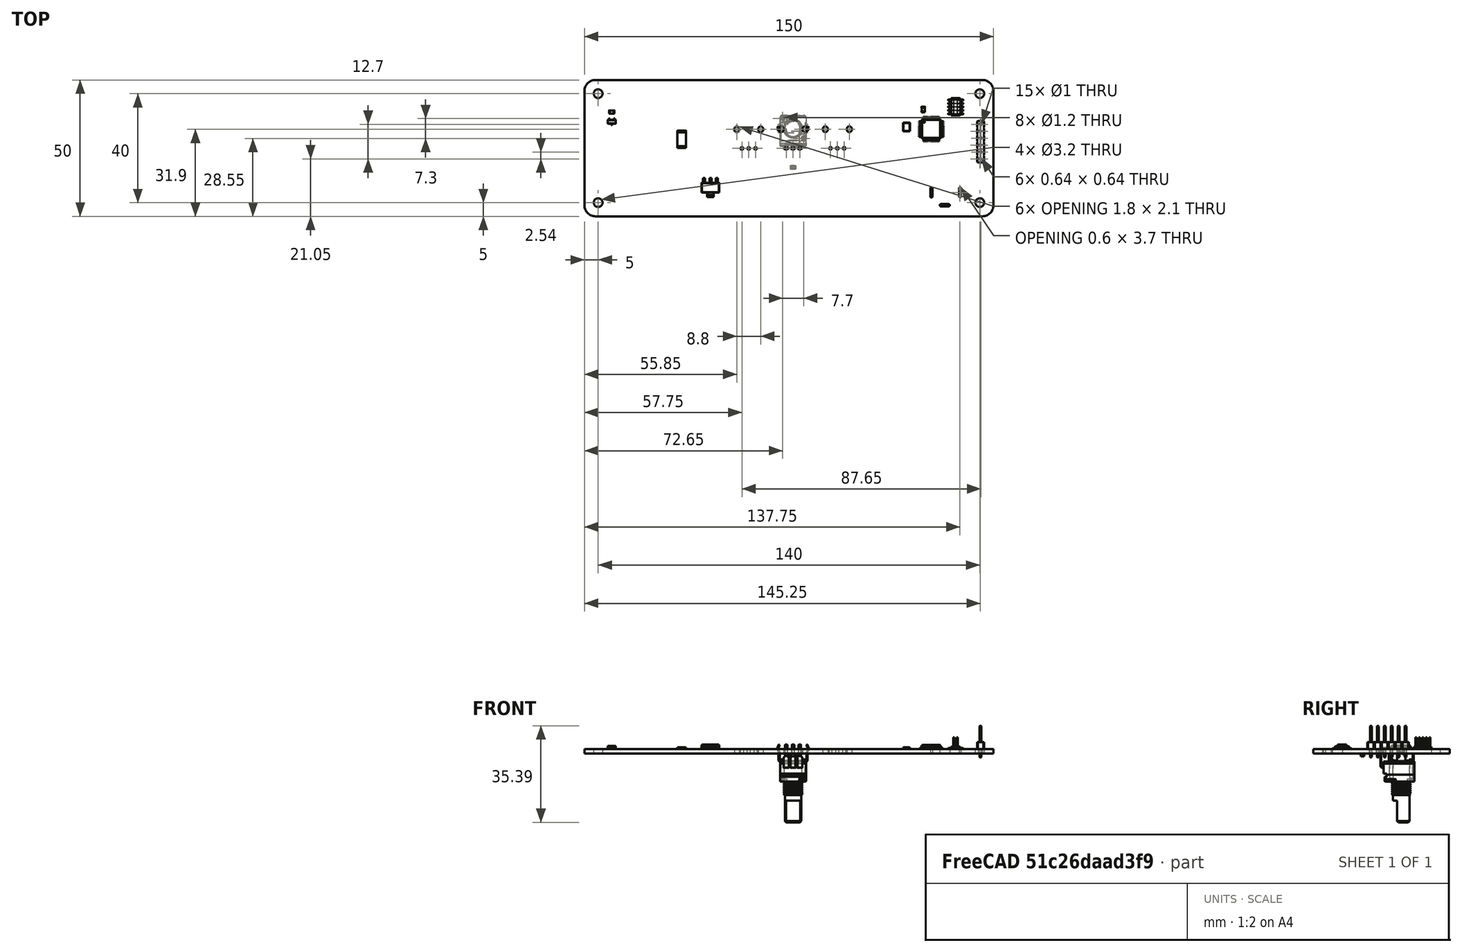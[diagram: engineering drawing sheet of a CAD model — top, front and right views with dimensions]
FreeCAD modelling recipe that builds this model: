
FCSTD DOCUMENT  (FreeCAD 0.19R24291 (Git))
Label: pcb
License: All rights reserved
LicenseURL: http://en.wikipedia.org/wiki/All_rights_reserved
objects: App::Link×47, Part::Feature×12, App::Part×5, PartDesign::CoordinateSystem×1, Sketcher::SketchObject×1
note: 14 computed .brp shape members not serialized (recipe doc carries the construction recipe); baked Part::Feature solids carry a one-line shape summary decoded from their .brp

FEATURE [PartDesign::CoordinateSystem] Local_CS_2cbe
  AttacherType = Attacher::AttachEngine3D
FEATURE [Part::Feature] Pcb_2cbe
  shape: bbox 150 x 50 x 1.6 mm, 83 faces (baked)
FEATURE [Sketcher::SketchObject] PCB_Sketch_2cbe
  FullyConstrained = false
  sketch-geometry (8):
    g0: LineSegment StartX=150 StartY=-46 StartZ=0 EndX=150 EndY=-4 EndZ=0
    g1: LineSegment StartX=4 StartY=-50 StartZ=0 EndX=146 EndY=-50 EndZ=0
    g2: LineSegment StartX=146 StartY=-4.4e-15 StartZ=0 EndX=4 EndY=0 EndZ=0
    g3: LineSegment StartX=0 StartY=-4 StartZ=0 EndX=4.4e-15 EndY=-46 EndZ=0
    g4: ArcOfCircle CenterX=146 CenterY=-46 CenterZ=0 NormalX=0 NormalY=0 NormalZ=-1 AngleXU=-3.14159 Radius=4 StartAngle=0 EndAngle=1.5708
    g5: ArcOfCircle CenterX=4 CenterY=-4 CenterZ=0 NormalX=0 NormalY=0 NormalZ=-1 AngleXU=1.06478e-07 Radius=4 StartAngle=0 EndAngle=1.5708
    g6: ArcOfCircle CenterX=146 CenterY=-4 CenterZ=0 NormalX=0 NormalY=0 NormalZ=-1 AngleXU=1.5708 Radius=4 StartAngle=0 EndAngle=1.5708
    g7: ArcOfCircle CenterX=4 CenterY=-46 CenterZ=0 NormalX=0 NormalY=0 NormalZ=-1 AngleXU=-1.5708 Radius=4 StartAngle=0 EndAngle=1.5708
  constraints (8):
    c: Coincident(g3,g7)
    c: Coincident(g3,g5)
    c: Coincident(g7,g1)
    c: Coincident(g2,g5)
    c: Coincident(g4,g1)
    c: Coincident(g6,g2)
    c: Coincident(g0,g4)
    c: Coincident(g0,g6)
FEATURE [App::Part] Board_Geoms_2cbe
  Group = -> [Local_CS_2cbe,Pcb_2cbe,PCB_Sketch_2cbe]
  Origin = -> Origin
FEATURE [Part::Feature] Shape  label="U3_SOT_223_9a0cac0f9152"
  Placement = pos=(46.1875,-39.5,0) rot=(0,0,-1;1.5708rad)
  shape: bbox 6.5 x 7 x 1.7 mm, 78 faces (baked)
FEATURE [Part::Feature] Shape001  label="R17_R_0805_2012Metric_1d3dcb9a6ad1"
  Placement = pos=(10,-11.75,0) rot=(0,0,1;3.14159rad)
  shape: bbox 2 x 1.2 x 0.45 mm, 26 faces (baked)
FEATURE [App::Link] R17_R_0805_2012Metric_1d3dcb9a6ad1_ln_  label="R11_R_0805_2012Metric_20203f5f4346"
  LinkPlacement = pos=(20.25,-11.75,0) rot=(0,0,1;3.14159rad)
  LinkedObject = -> Shape001
  Placement = pos=(20.25,-11.75,0) rot=(0,0,1;3.14159rad)
FEATURE [Part::Feature] Shape002  label="R3_R_2512_6332Metric_9794fe5d1dc9"
  Placement = pos=(35.6875,-21.75,0) rot=(0,0,1;1.5708rad)
  shape: bbox 3.2 x 6.3 x 0.6 mm, 26 faces (baked)
FEATURE [App::Link] R17_R_0805_2012Metric_1d3dcb9a6ad1_ln_001  label="R14_R_0805_2012Metric_fdd2a95da5c4"
  LinkPlacement = pos=(15,-11.75,0) rot=(0,0,1;3.14159rad)
  LinkedObject = -> Shape001
  Placement = pos=(15,-11.75,0) rot=(0,0,1;3.14159rad)
FEATURE [Part::Feature] Shape003  label="C5_C_0805_2012Metric_e73408091e88"
  Placement = pos=(124.25,-10.8,0) rot=(0,0,1;1.5708rad)
  shape: bbox 1.25 x 2 x 1.25 mm, 28 faces (baked)
FEATURE [App::Link] R17_R_0805_2012Metric_1d3dcb9a6ad1_ln_002  label="R25_R_0805_2012Metric_45299f0951f4"
  LinkPlacement = pos=(41.1875,-9.25,0) rot=(0,0,1;0rad)
  LinkedObject = -> Shape001
  Placement = pos=(41.1875,-9.25,0) rot=(0,0,1;0rad)
FEATURE [App::Link] R3_R_2512_6332Metric_9794fe5d1dc9_ln_  label="R21_R_2512_6332Metric_ab6f071dc77f"
  LinkPlacement = pos=(51.4375,-21.75,0) rot=(0,0,1;1.5708rad)
  LinkedObject = -> Shape002
  Placement = pos=(51.4375,-21.75,0) rot=(0,0,1;1.5708rad)
FEATURE [Part::Feature] Shape004  label="Q6_SOT_23_5775dbb67c7d"
  Placement = pos=(10,-15.3125,0) rot=(0,0,-1;1.5708rad)
  shape: bbox 3 x 2.5 x 1.2 mm, 76 faces (baked)
FEATURE [App::Link] R17_R_0805_2012Metric_1d3dcb9a6ad1_ln_003  label="R20_R_0805_2012Metric_a0866f91f469"
  LinkPlacement = pos=(51.4375,-11.75,0) rot=(0,0,1;3.14159rad)
  LinkedObject = -> Shape001
  Placement = pos=(51.4375,-11.75,0) rot=(0,0,1;3.14159rad)
FEATURE [App::Link] R17_R_0805_2012Metric_1d3dcb9a6ad1_ln_004  label="R22_R_0805_2012Metric_833be10c83fc"
  LinkPlacement = pos=(46.1875,-9.25,0) rot=(0,0,1;0rad)
  LinkedObject = -> Shape001
  Placement = pos=(46.1875,-9.25,0) rot=(0,0,1;0rad)
FEATURE [App::Link] R3_R_2512_6332Metric_9794fe5d1dc9_ln_001  label="R18_R_2512_6332Metric_0a6bf79341f9"
  LinkPlacement = pos=(10,-21.75,0) rot=(0,0,1;1.5708rad)
  LinkedObject = -> Shape002
  Placement = pos=(10,-21.75,0) rot=(0,0,1;1.5708rad)
FEATURE [App::Link] R17_R_0805_2012Metric_1d3dcb9a6ad1_ln_005  label="R19_R_0805_2012Metric_baaa63a81d46"
  LinkPlacement = pos=(51.4375,-9.25,0) rot=(0,0,1;0rad)
  LinkedObject = -> Shape001
  Placement = pos=(51.4375,-9.25,0) rot=(0,0,1;0rad)
FEATURE [App::Link] R17_R_0805_2012Metric_1d3dcb9a6ad1_ln_006  label="R10_R_0805_2012Metric_2b905bbe2cce"
  LinkPlacement = pos=(20.25,-9.25,0) rot=(0,0,1;0rad)
  LinkedObject = -> Shape001
  Placement = pos=(20.25,-9.25,0) rot=(0,0,1;0rad)
FEATURE [App::Link] C5_C_0805_2012Metric_e73408091e88_ln_  label="C1_C_0805_2012Metric_e32d38fff6b7"
  LinkPlacement = pos=(118.25,-20.8,0) rot=(0,0,1;3.14159rad)
  LinkedObject = -> Shape003
  Placement = pos=(118.25,-20.8,0) rot=(0,0,1;3.14159rad)
FEATURE [App::Link] C5_C_0805_2012Metric_e73408091e88_ln_001  label="C7_C_0805_2012Metric_6d577f5282f8"
  LinkPlacement = pos=(132,-23.5,0) rot=(0,0,-1;1.5708rad)
  LinkedObject = -> Shape003
  Placement = pos=(132,-23.5,0) rot=(0,0,-1;1.5708rad)
FEATURE [App::Link] Q6_SOT_23_5775dbb67c7d_ln_  label="Q9_SOT_23_ff8b5d4c65c8"
  LinkPlacement = pos=(41.1875,-15.3125,0) rot=(0,0,-1;1.5708rad)
  LinkedObject = -> Shape004
  Placement = pos=(41.1875,-15.3125,0) rot=(0,0,-1;1.5708rad)
FEATURE [App::Link] U3_SOT_223_9a0cac0f9152_ln_  label="U4_SOT_223_e91abe411a87"
  LinkPlacement = pos=(137.85,-32.85,0) rot=(0,0,1;0rad)
  LinkedObject = -> Shape
  Placement = pos=(137.85,-32.85,0) rot=(0,0,1;0rad)
FEATURE [App::Link] C5_C_0805_2012Metric_e73408091e88_ln_002  label="C4_C_0805_2012Metric_672b2dcb80fa"
  LinkPlacement = pos=(137,-23.5,0) rot=(0,0,-1;1.5708rad)
  LinkedObject = -> Shape003
  Placement = pos=(137,-23.5,0) rot=(0,0,-1;1.5708rad)
FEATURE [App::Link] Q6_SOT_23_5775dbb67c7d_ln_001  label="Q7_SOT_23_17abb1841a15"
  LinkPlacement = pos=(51.4375,-15.3125,0) rot=(0,0,-1;1.5708rad)
  LinkedObject = -> Shape004
  Placement = pos=(51.4375,-15.3125,0) rot=(0,0,-1;1.5708rad)
FEATURE [App::Link] R3_R_2512_6332Metric_9794fe5d1dc9_ln_002  label="R15_R_2512_6332Metric_e9b0cec35db8"
  LinkPlacement = pos=(15,-21.75,0) rot=(0,0,1;1.5708rad)
  LinkedObject = -> Shape002
  Placement = pos=(15,-21.75,0) rot=(0,0,1;1.5708rad)
FEATURE [App::Link] R3_R_2512_6332Metric_9794fe5d1dc9_ln_003  label="R27_R_2512_6332Metric_f9a6948b6ee0"
  LinkPlacement = pos=(41.1875,-21.75,0) rot=(0,0,1;1.5708rad)
  LinkedObject = -> Shape002
  Placement = pos=(41.1875,-21.75,0) rot=(0,0,1;1.5708rad)
FEATURE [App::Link] R17_R_0805_2012Metric_1d3dcb9a6ad1_ln_007  label="R2_R_0805_2012Metric_4f3d63e405d4"
  LinkPlacement = pos=(35.6875,-11.75,0) rot=(0,0,1;3.14159rad)
  LinkedObject = -> Shape001
  Placement = pos=(35.6875,-11.75,0) rot=(0,0,1;3.14159rad)
FEATURE [App::Link] U3_SOT_223_9a0cac0f9152_ln_001  label="U1_SOT_223_7fe5ee313dd0"
  LinkPlacement = pos=(30.4375,-39.5,0) rot=(0,0,-1;1.5708rad)
  LinkedObject = -> Shape
  Placement = pos=(30.4375,-39.5,0) rot=(0,0,-1;1.5708rad)
FEATURE [App::Link] R3_R_2512_6332Metric_9794fe5d1dc9_ln_004  label="R9_R_2512_6332Metric_ee968ef2a15d"
  LinkPlacement = pos=(25.4375,-21.75,0) rot=(0,0,1;1.5708rad)
  LinkedObject = -> Shape002
  Placement = pos=(25.4375,-21.75,0) rot=(0,0,1;1.5708rad)
FEATURE [App::Link] R17_R_0805_2012Metric_1d3dcb9a6ad1_ln_008  label="R28_R_0805_2012Metric_0c4fd54d4787"
  LinkPlacement = pos=(130.5,-8.4125,0) rot=(0,0,1;1.5708rad)
  LinkedObject = -> Shape001
  Placement = pos=(130.5,-8.4125,0) rot=(0,0,1;1.5708rad)
FEATURE [App::Link] R3_R_2512_6332Metric_9794fe5d1dc9_ln_005  label="R6_R_2512_6332Metric_ac73445917ac"
  LinkPlacement = pos=(30.4375,-21.75,0) rot=(0,0,1;1.5708rad)
  LinkedObject = -> Shape002
  Placement = pos=(30.4375,-21.75,0) rot=(0,0,1;1.5708rad)
FEATURE [App::Link] R17_R_0805_2012Metric_1d3dcb9a6ad1_ln_009  label="R8_R_0805_2012Metric_5f2fab4355a1"
  LinkPlacement = pos=(25.4375,-11.75,0) rot=(0,0,1;3.14159rad)
  LinkedObject = -> Shape001
  Placement = pos=(25.4375,-11.75,0) rot=(0,0,1;3.14159rad)
FEATURE [App::Link] R17_R_0805_2012Metric_1d3dcb9a6ad1_ln_010  label="R29_R_0805_2012Metric_2565f2ac43fa"
  LinkPlacement = pos=(135.25,-20,0) rot=(0,0,1;0rad)
  LinkedObject = -> Shape001
  Placement = pos=(135.25,-20,0) rot=(0,0,1;0rad)
FEATURE [App::Link] R17_R_0805_2012Metric_1d3dcb9a6ad1_ln_011  label="R23_R_0805_2012Metric_bd181034dc98"
  LinkPlacement = pos=(46.1875,-11.75,0) rot=(0,0,1;3.14159rad)
  LinkedObject = -> Shape001
  Placement = pos=(46.1875,-11.75,0) rot=(0,0,1;3.14159rad)
FEATURE [App::Link] C5_C_0805_2012Metric_e73408091e88_ln_003  label="C8_C_0805_2012Metric_dd346f149829"
  LinkPlacement = pos=(131.25,-34.8,0) rot=(0,0,-1;1.5708rad)
  LinkedObject = -> Shape003
  Placement = pos=(131.25,-34.8,0) rot=(0,0,-1;1.5708rad)
FEATURE [Part::Feature] Shape005  label="Y1_Crystal_SMD_3225-4Pin_3.2x2.5mm_c7f48e4b8aec"
  Placement = pos=(118.15,-17.2,0) rot=(0,0,-1;1.5708rad)
  shape: bbox 2.501 x 3.2 x 0.64 mm, 28 faces (baked)
FEATURE [Part::Feature] Shape006  label="J5_PinHeader_2x05_P127mm_Vertical_SMD_d72e22a41a84"
  Placement = pos=(136.15,-9.85,0) rot=(0,0,1;3.14159rad)
  shape: bbox 5.57 x 6.35 x 4.4 mm, 224 faces (baked)
FEATURE [App::Link] C5_C_0805_2012Metric_e73408091e88_ln_004  label="C2_C_0805_2012Metric_1cae6d697659"
  LinkPlacement = pos=(118.2,-13.8,0) rot=(0,0,1;3.14159rad)
  LinkedObject = -> Shape003
  Placement = pos=(118.2,-13.8,0) rot=(0,0,1;3.14159rad)
FEATURE [Part::Feature] Shape007  label="J6_PinHeader_1x06_P254mm_Vertical_fd384cb3f28f"
  Placement = pos=(145.25,-16.25,0) rot=(0,0,1;0rad)
  shape: bbox 2.54 x 15.24 x 11.54 mm, 148 faces (baked)
FEATURE [App::Link] R3_R_2512_6332Metric_9794fe5d1dc9_ln_006  label="R24_R_2512_6332Metric_24b84e4ca8f6"
  LinkPlacement = pos=(46.1875,-21.75,0) rot=(0,0,1;1.5708rad)
  LinkedObject = -> Shape002
  Placement = pos=(46.1875,-21.75,0) rot=(0,0,1;1.5708rad)
FEATURE [App::Link] R17_R_0805_2012Metric_1d3dcb9a6ad1_ln_012  label="R26_R_0805_2012Metric_8c81e733eccd"
  LinkPlacement = pos=(41.1875,-11.75,0) rot=(0,0,1;3.14159rad)
  LinkedObject = -> Shape001
  Placement = pos=(41.1875,-11.75,0) rot=(0,0,1;3.14159rad)
FEATURE [App::Link] Q6_SOT_23_5775dbb67c7d_ln_002  label="Q8_SOT_23_1fa8c5138ddd"
  LinkPlacement = pos=(46.1875,-15.3125,0) rot=(0,0,-1;1.5708rad)
  LinkedObject = -> Shape004
  Placement = pos=(46.1875,-15.3125,0) rot=(0,0,-1;1.5708rad)
FEATURE [App::Link] Q6_SOT_23_5775dbb67c7d_ln_003  label="Q5_SOT_23_a44b0229e8dc"
  LinkPlacement = pos=(15,-15.3125,0) rot=(0,0,-1;1.5708rad)
  LinkedObject = -> Shape004
  Placement = pos=(15,-15.3125,0) rot=(0,0,-1;1.5708rad)
FEATURE [App::Link] C5_C_0805_2012Metric_e73408091e88_ln_005  label="C3_C_0805_2012Metric_4d4c3b780c7d"
  LinkPlacement = pos=(134.5,-23.5,0) rot=(0,0,-1;1.5708rad)
  LinkedObject = -> Shape003
  Placement = pos=(134.5,-23.5,0) rot=(0,0,-1;1.5708rad)
FEATURE [App::Link] Q6_SOT_23_5775dbb67c7d_ln_004  label="Q1_SOT_23_beec94fd2b5f"
  LinkPlacement = pos=(35.6875,-15.3125,0) rot=(0,0,-1;1.5708rad)
  LinkedObject = -> Shape004
  Placement = pos=(35.6875,-15.3125,0) rot=(0,0,-1;1.5708rad)
FEATURE [App::Link] R17_R_0805_2012Metric_1d3dcb9a6ad1_ln_013  label="R5_R_0805_2012Metric_c2fdd37d7649"
  LinkPlacement = pos=(30.4375,-11.75,0) rot=(0,0,1;3.14159rad)
  LinkedObject = -> Shape001
  Placement = pos=(30.4375,-11.75,0) rot=(0,0,1;3.14159rad)
FEATURE [App::Link] R17_R_0805_2012Metric_1d3dcb9a6ad1_ln_014  label="R30_R_0805_2012Metric_f70d4868c63e"
  LinkPlacement = pos=(126.5,-10.75,0) rot=(0,0,1;1.5708rad)
  LinkedObject = -> Shape001
  Placement = pos=(126.5,-10.75,0) rot=(0,0,1;1.5708rad)
FEATURE [App::Link] R17_R_0805_2012Metric_1d3dcb9a6ad1_ln_015  label="R4_R_0805_2012Metric_136d3f58f10c"
  LinkPlacement = pos=(30.4375,-9.25,0) rot=(0,0,1;0rad)
  LinkedObject = -> Shape001
  Placement = pos=(30.4375,-9.25,0) rot=(0,0,1;0rad)
FEATURE [App::Link] R17_R_0805_2012Metric_1d3dcb9a6ad1_ln_016  label="R7_R_0805_2012Metric_8f9a76bd2325"
  LinkPlacement = pos=(25.4375,-9.25,0) rot=(0,0,1;0rad)
  LinkedObject = -> Shape001
  Placement = pos=(25.4375,-9.25,0) rot=(0,0,1;0rad)
FEATURE [App::Link] R17_R_0805_2012Metric_1d3dcb9a6ad1_ln_017  label="R1_R_0805_2012Metric_98cd4f012b1e"
  LinkPlacement = pos=(35.6875,-9.25,0) rot=(0,0,1;0rad)
  LinkedObject = -> Shape001
  Placement = pos=(35.6875,-9.25,0) rot=(0,0,1;0rad)
FEATURE [App::Link] R17_R_0805_2012Metric_1d3dcb9a6ad1_ln_018  label="R13_R_0805_2012Metric_5c4c1cf987fe"
  LinkPlacement = pos=(15,-9.25,0) rot=(0,0,1;0rad)
  LinkedObject = -> Shape001
  Placement = pos=(15,-9.25,0) rot=(0,0,1;0rad)
FEATURE [App::Link] R3_R_2512_6332Metric_9794fe5d1dc9_ln_007  label="R12_R_2512_6332Metric_5527fe2de375"
  LinkPlacement = pos=(20.25,-21.75,0) rot=(0,0,1;1.5708rad)
  LinkedObject = -> Shape002
  Placement = pos=(20.25,-21.75,0) rot=(0,0,1;1.5708rad)
FEATURE [App::Link] Q6_SOT_23_5775dbb67c7d_ln_005  label="Q4_SOT_23_f877d4d9137f"
  LinkPlacement = pos=(20.25,-15.3125,0) rot=(0,0,-1;1.5708rad)
  LinkedObject = -> Shape004
  Placement = pos=(20.25,-15.3125,0) rot=(0,0,-1;1.5708rad)
FEATURE [App::Link] Q6_SOT_23_5775dbb67c7d_ln_006  label="Q2_SOT_23_ab36755b93e8"
  LinkPlacement = pos=(30.4375,-15.3125,0) rot=(0,0,-1;1.5708rad)
  LinkedObject = -> Shape004
  Placement = pos=(30.4375,-15.3125,0) rot=(0,0,-1;1.5708rad)
FEATURE [App::Link] R17_R_0805_2012Metric_1d3dcb9a6ad1_ln_019  label="R16_R_0805_2012Metric_7f67fb58ddc2"
  LinkPlacement = pos=(10,-9.25,0) rot=(0,0,1;0rad)
  LinkedObject = -> Shape001
  Placement = pos=(10,-9.25,0) rot=(0,0,1;0rad)
FEATURE [App::Link] C5_C_0805_2012Metric_e73408091e88_ln_006  label="C6_C_0805_2012Metric_12e3dac60f4f"
  LinkPlacement = pos=(122,-12.8,0) rot=(0,0,1;1.5708rad)
  LinkedObject = -> Shape003
  Placement = pos=(122,-12.8,0) rot=(0,0,1;1.5708rad)
FEATURE [App::Link] Q6_SOT_23_5775dbb67c7d_ln_007  label="Q3_SOT_23_4412773ee660"
  LinkPlacement = pos=(25.4375,-15.3125,0) rot=(0,0,-1;1.5708rad)
  LinkedObject = -> Shape004
  Placement = pos=(25.4375,-15.3125,0) rot=(0,0,-1;1.5708rad)
FEATURE [Part::Feature] Shape008  label="U5_LQFP_48_7x7mm_P05mm_4cf980e7d14d"
  Placement = pos=(127.2,-17.96,0) rot=(0,0,1;0rad)
  shape: bbox 9 x 9 x 1.5 mm, 764 faces (baked)
FEATURE [App::Link] U3_SOT_223_9a0cac0f9152_ln_002  label="U2_SOT_223_248f1c736c53"
  LinkPlacement = pos=(15,-39.5,0) rot=(0,0,-1;1.5708rad)
  LinkedObject = -> Shape
  Placement = pos=(15,-39.5,0) rot=(0,0,-1;1.5708rad)
FEATURE [App::Link] C5_C_0805_2012Metric_e73408091e88_ln_007  label="C9_C_0805_2012Metric_4c2c7760fe1f"
  LinkPlacement = pos=(131.25,-31.05,0) rot=(0,0,1;1.5708rad)
  LinkedObject = -> Shape003
  Placement = pos=(131.25,-31.05,0) rot=(0,0,1;1.5708rad)
FEATURE [App::Part] Top_2cbe
  Group = -> [Shape,Shape001,R17_R_0805_2012Metric_1d3dcb9a6ad1_ln_,Shape002,R17_R_0805_2012Metric_1d3dcb9a6ad1_ln_001,Shape003,R17_R_0805_2012Metric_1d3dcb9a6ad1_ln_002,R3_R_2512_6332Metric_9794fe5d1dc9_ln_,Shape004,R17_R_0805_2012Metric_1d3dcb9a6ad1_ln_003,R17_R_0805_2012Metric_1d3dcb9a6ad1_ln_004,R3_R_2512_6332Metric_9794fe5d1dc9_ln_001,R17_R_0805_2012Metric_1d3dcb9a6ad1_ln_005,+43 more]
  Origin = -> Origin003
FEATURE [Part::Feature] Shape009  label="RV2_RD901F-40-15F_f07eda9b56f9[2]"
  Placement = pos=(76.5,-17.8,-1.85) rot=(0,1,0;3.14159rad)
  shape: bbox 11.73 x 12.51 x 28.51 mm, 264 faces, 9 solids (baked)
FEATURE [Part::Feature] Shape010  label="D1_LED_0805_2012Metric_c4725b8218e0"
  Placement = pos=(76.5,-32,-1.6) rot=(1,0,0;3.14159rad)
  shape: bbox 2 x 1.25 x 1.1 mm, 50 faces (baked)
FEATURE [App::Part] Bot_2cbe
  Group = -> [Shape009,Shape010]
  Origin = -> Origin004
FEATURE [App::Part] Step_Models_2cbe
  Group = -> [Top_2cbe,Bot_2cbe]
  Origin = -> Origin002
FEATURE [App::Part] Board_2cbe  label="controller"
  Group = -> [Board_Geoms_2cbe,Step_Models_2cbe]
  Origin = -> Origin001
